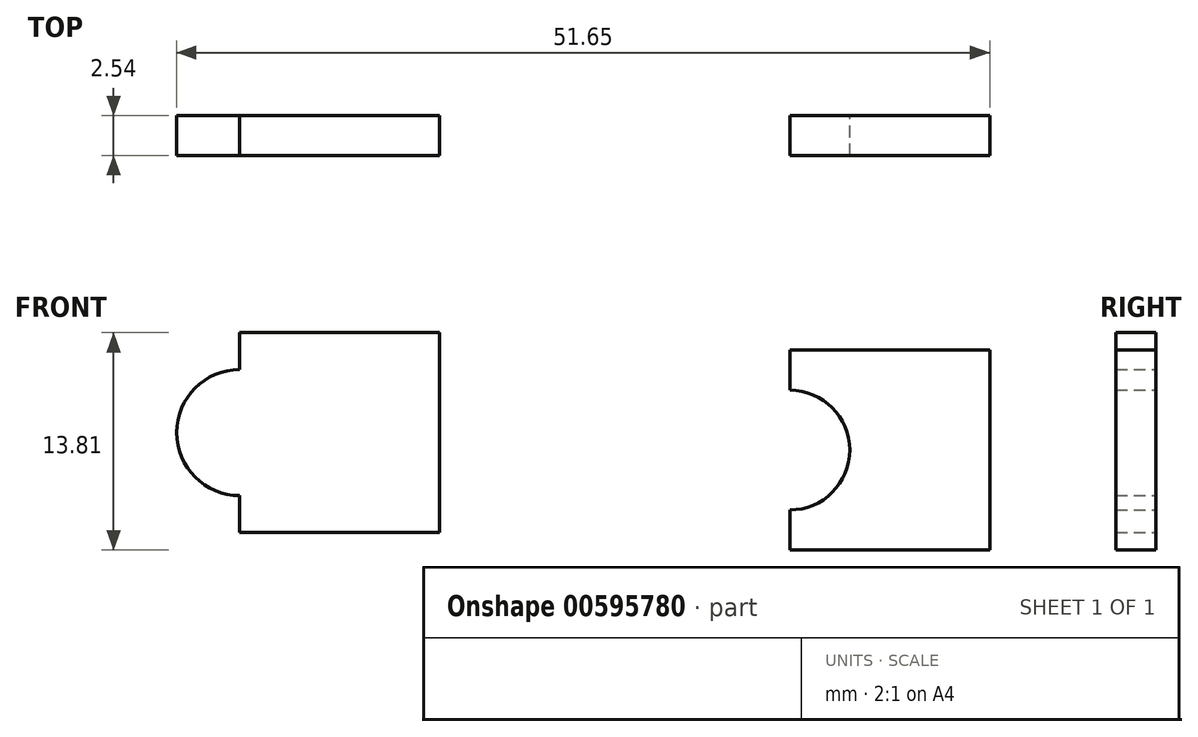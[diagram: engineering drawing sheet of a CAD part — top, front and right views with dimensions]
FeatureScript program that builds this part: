
annotation { "Feature Type Name" : "Feature", "Feature Type Description" : "" }
export const myFeature = defineFeature(function(context is Context, id is Id, definition is map)
    precondition{}
    {
        {
            var Q0;
            Q0=qCreatedBy(makeId("Front.planeOp"),FACE);
            var sketch = newSketch(context, id + "F0", { "sketchPlane" : qUnion([Q0])});
            skLineSegment(sketch, "E0", {"start": v(-62.88, 58.17) * mm, "end": v(-50.18, 58.17) * mm});
            skLineSegment(sketch, "E1", {"start": v(-50.18, 58.17) * mm, "end": v(-50.18, 58.17) * mm});
            skLineSegment(sketch, "E2", {"start": v(-50.18, 45.47) * mm, "end": v(-52.47, 45.47) * mm});
            skLineSegment(sketch, "E3", {"start": v(-62.88, 45.47) * mm, "end": v(-62.88, 58.17) * mm});
            skLineSegment(sketch, "E4.trimOffspring", {"start": v(-50.18, 45.47) * mm, "end": v(-50.18, 45.47) * mm});
            skLineSegment(sketch, "E5.trimOffspring", {"start": v(-60.6, 45.47) * mm, "end": v(-62.88, 45.47) * mm});
            skLineSegment(sketch, "E6", {"start": v(-50.18, 58.17) * mm, "end": v(-50.18, 56.14) * mm});
            skLineSegment(sketch, "E7.trimOffspring", {"start": v(-50.18, 47.5) * mm, "end": v(-50.18, 45.47) * mm});
            skLineSegment(sketch, "E8", {"start": v(-56.53, 45.47) * mm, "end": v(-52.47, 45.47) * mm});
            skLineSegment(sketch, "E9", {"start": v(-60.6, 45.47) * mm, "end": v(-56.53, 45.47) * mm});
            skLineSegment(sketch, "E10", {"start": v(-50.18, 56.14) * mm, "end": v(-50.18, 47.5) * mm});
            skArc(sketch, "E11", {"start": v(-50.18, 55.76) * mm, "mid": v(-46.25, 51.82) * mm, "end": v(-50.18, 47.88) * mm});
            skArc(sketch, "E12", {"start": v(-52.66, 45.47) * mm, "mid": v(-56.53, 41.6) * mm, "end": v(-60.4, 45.47) * mm});
            skArc(sketch, "E13", {"start": v(-62.88, 55.82) * mm, "mid": v(-66.89, 51.82) * mm, "end": v(-62.88, 47.82) * mm});
            skSolve(sketch);
        }
        {
            var Q0;
            Q0=qCreatedBy(makeId("Front.planeOp"),FACE);
            var sketch = newSketch(context, id + "F1", { "sketchPlane" : qUnion([Q0])});
            skLineSegment(sketch, "E14", {"start": v(-27.94, 57.06) * mm, "end": v(-15.24, 57.06) * mm});
            skLineSegment(sketch, "E15", {"start": v(-15.24, 57.06) * mm, "end": v(-15.24, 44.36) * mm});
            skLineSegment(sketch, "E16", {"start": v(-15.24, 44.36) * mm, "end": v(-27.94, 44.36) * mm});
            skLineSegment(sketch, "E17", {"start": v(-27.94, 44.36) * mm, "end": v(-27.94, 46.9) * mm});
            skArc(sketch, "E18", {"start": v(-27.94, 54.52) * mm, "mid": v(-24.13, 50.71) * mm, "end": v(-27.94, 46.9) * mm});
            skLineSegment(sketch, "E19.trimOffspring", {"start": v(-27.94, 54.52) * mm, "end": v(-27.94, 57.06) * mm});
            skSolve(sketch);
        }
        {
            var Q0;
            Q0 = qSketchRegion(id + "F1", true);
            extrude(context, id + "F2", {"entities" : qUnion([Q0]), "depth" : 2.54 * mm, "offsetDistance" : 25.4 * mm});
        }
        {
            var Q0;
            {var subQ10=sQuery(id+"F0.wireOp",EDGE,"E0");Q0=makeQuery(id+"F0.imprint","IMPRINT",FACE,{"disambiguationData":[TD([[makeQuery(id+"F0.imprint","IMPRINT",EDGE,{"derivedFrom":subQ10}),-1.0]])]});}
            var Q1;
            {var subQ0=sQuery(id+"F0.wireOp",EDGE,"E13");Q1=makeQuery(id+"F0.imprint","IMPRINT",FACE,{"disambiguationData":[TD([[makeQuery(id+"F0.imprint","IMPRINT",EDGE,{"derivedFrom":subQ0}),1.0]])]});}
            var Q2;
            {var subQ0=sQuery(id+"F0.wireOp",EDGE,"E11");Q2=makeQuery(id+"F0.imprint","IMPRINT",FACE,{"disambiguationData":[TD([[makeQuery(id+"F0.imprint","IMPRINT",EDGE,{"derivedFrom":subQ0}),-1.0]])]});}
            var Q3;
            {var subQ3=sQuery(id+"F0.wireOp",EDGE,"E12");Q3=makeQuery(id+"F0.imprint","IMPRINT",FACE,{"disambiguationData":[TD([[makeQuery(id+"F0.imprint","IMPRINT",EDGE,{"derivedFrom":subQ3}),-1.0]])]});}
            extrude(context, id + "F3", {"entities" : qUnion([Q0, Q1, Q2, Q3]), "depth" : 2.54 * mm, "offsetDistance" : 25.4 * mm});
        }
    });
